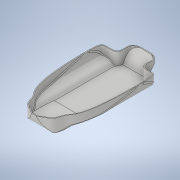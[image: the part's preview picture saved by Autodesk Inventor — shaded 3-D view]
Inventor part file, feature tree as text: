
AUTODESK INVENTOR PART (.ipt)
format: ipt  version: 2020.1 (Build 241239000, 239)  size: 1,449,472 bytes
history: native  units: mm
features: other x8, extrude x5, sketch x3, surface_op x2, delete_face x1, plane x1, split x1, chamfer x1, shell x1
ambient origin geometry x8: Origin, YZ Plane, XZ Plane, XY Plane, X Axis, Y Axis, Z Axis, Center Point
bodies: Body1 (feature_tree), Body2 (feature_tree), Body3 (feature_tree), Body4 (feature_tree), Body5 (feature_tree)
feature tree (23):
  other  "deck.ipt"
  other  "CrossSection1"
  other  "CrossSection2"
  delete_face  "Delete Face1"
  surface_op  "Extend3"
  plane  "Work Plane1"
  sketch  "Sketch22"  dims[d2=10.0mm d3=300.0mm d4=0.0mm]
  sketch  "Sketch24"  dims[d66=-41.0mm]
  surface_op  "Sculpt7"
  extrude  "Extrusion9"  Depth=300.0mm TaperAngle=0.0deg
  split  "Split3"
  chamfer  "Chamfer1"  Distance=5.0mm
  shell  "Shell2"  Thickness=37.0mm
  other  "Srf1"
  other  "Front Profile"
  sketch  "Sketch25"  dims[d110=91.75mm d290=5.0mm d293=37.0mm d294=186.0mm d295=32.0mm d296=90.0mm d297=5.0mm d298=14.0mm d299=3.0mm d300=3.0mm d303=62.0mm d304=70.0mm d305=38.0mm d306=105.0mm d307=14.0mm d308=500.0mm d309=0.0mm d310=250.0mm d311=0.0mm d312=50.0mm d313=0.0mm d314=167.75mm d315=0.0mm d317=0.5mm d318=2.0mm d319=0.0mm d320=20.0mm d321=3.0mm d322=2.0mm d323=45.0deg d324=0.5mm d325=2.0mm d326=114.0mm d327=20.0mm d328=2.5mm]
  other  "Srf32"
  other  "Srf33"
  other  "Srf34"
  extrude  "ExtrusionSrf1"  Depth=186.0mm
  extrude  "ExtrusionSrf9"  Depth=32.0mm
  extrude  "ExtrusionSrf10"  Depth=90.0mm
  extrude  "ExtrusionSrf11"  Depth=5.0mm
